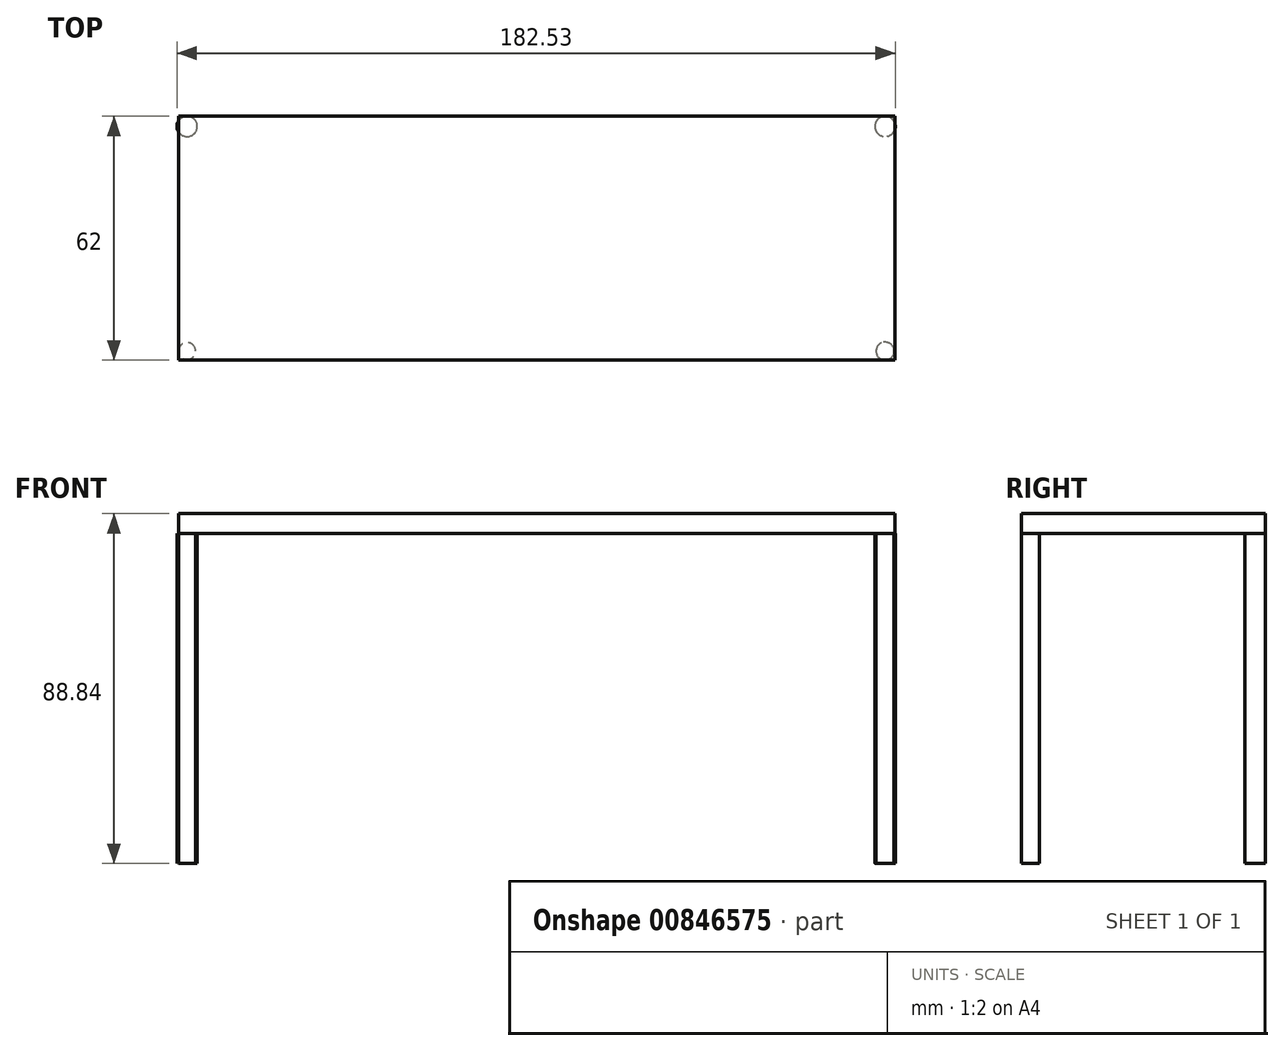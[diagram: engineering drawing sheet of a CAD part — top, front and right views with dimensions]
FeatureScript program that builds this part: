
annotation { "Feature Type Name" : "Feature", "Feature Type Description" : "" }
export const myFeature = defineFeature(function(context is Context, id is Id, definition is map)
    precondition{}
    {
        {
            var Q0;
            Q0=qCreatedBy(makeId("Top.planeOp"),FACE);
            var sketch = newSketch(context, id + "F0", { "sketchPlane" : qUnion([Q0])});
            skLineSegment(sketch, "E0.bottom", {"start": v(-93.55, 31) * mm, "end": v(88.45, 31) * mm});
            skLineSegment(sketch, "E0.top", {"start": v(-93.55, -31) * mm, "end": v(88.45, -31) * mm});
            skLineSegment(sketch, "E0.left", {"start": v(-93.55, 31) * mm, "end": v(-93.55, -31) * mm});
            skLineSegment(sketch, "E0.right", {"start": v(88.45, 31) * mm, "end": v(88.45, -31) * mm});
            skPoint(sketch, "E0.middle", {"position": v(-2.55, 0) * mm});
            skSolve(sketch);
        }
        {
            var Q0;
            Q0 = qSketchRegion(id + "F0", true);
            extrude(context, id + "F1", {"entities" : qUnion([Q0]), "depth" : 5 * mm, "offsetDistance" : 25 * mm});
        }
        {
            var Q0;
            Q0=makeQuery(id+"F1.opExtrude","CAP_FACE",FACE,{"disambiguationData":[OSD([sQuery(id+"F0.wireOp",EDGE,"E0.bottom"),sQuery(id+"F0.wireOp",EDGE,"E0.top"),sQuery(id+"F0.wireOp",EDGE,"E0.left"),sQuery(id+"F0.wireOp",EDGE,"E0.right")])],"isStart":true});
            var sketch = newSketch(context, id + "F2", { "sketchPlane" : qUnion([Q0])});
            skCircle(sketch, "E1", {"center": v(-91.37, 28.7) * mm, "radius": 2.18 * mm});
            skCircle(sketch, "E2", {"center": v(-91.37, -28.4) * mm, "radius": 2.6 * mm});
            skCircle(sketch, "E3", {"center": v(85.96, -28.4) * mm, "radius": 2.6 * mm});
            skCircle(sketch, "E4", {"center": v(85.96, 28.7) * mm, "radius": 2.3 * mm});
            skSolve(sketch);
        }
        {
            var Q0;
            Q0 = qSketchRegion(id + "F2", true);
            extrude(context, id + "F3", {"entities" : qUnion([Q0]), "operationType" : NewBodyOperationType.ADD, "depth" : 83.84 * mm, "offsetDistance" : 25 * mm});
        }
    });
